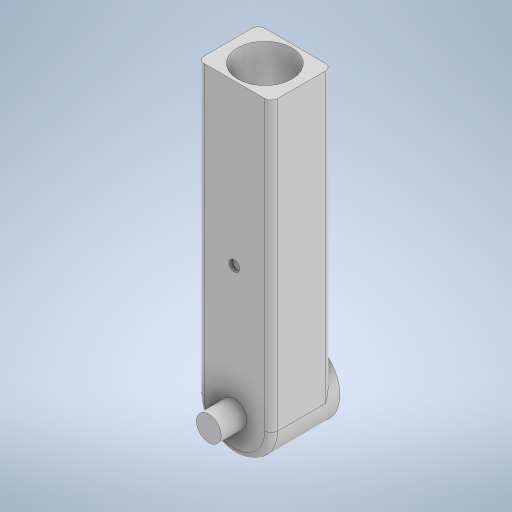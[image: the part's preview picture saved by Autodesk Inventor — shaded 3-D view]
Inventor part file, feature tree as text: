
AUTODESK INVENTOR PART (.ipt)
format: ipt  version: 2023 (Build 270158000, 158)  size: 334,848 bytes
history: native  units: in
note: dims shown in document units (in); Inventor stores cm internally (conversion verified against a paired STEP export)
features: extrude x8, sketch x8, fillet x1
ambient origin geometry x8: Origin, YZ Plane, XZ Plane, XY Plane, X Axis, Y Axis, Z Axis, Center Point
bodies: Solid1 (feature_tree)
feature tree (17):
  extrude  "Extrusion1"  Depth=1.0236in TaperAngle=0.0deg
  extrude  "Extrusion2"  Depth=3.1496in TaperAngle=0.0deg
  extrude  "Extrusion3"  Depth=0.9055in
  extrude  "Extrusion4"  Depth=0.2756in
  extrude  "Extrusion5"  Depth=0.3071in
  extrude  "Extrusion7"  Depth=0.6299in
  extrude  "Extrusion8"  Depth=0.5906in
  fillet  "Fillet2"  Radius=0.1969in
  extrude  "Extrusion9"  Depth=0.0787in
  sketch  "Sketch1"  dims[d0=0.9055in d1=1.0236in d2=0.0in]
  sketch  "Sketch2"  dims[d5=3.5433in d6=0.0in d8=3.1496in d9=0.0in]
  sketch  "Sketch3"  dims[d10=0.3071in d11=0.9055in]
  sketch  "Sketch4"  dims[d12=0.2756in d13=0.0in d15=0.2756in]
  sketch  "Sketch5"  dims[d16=0.0394in d17=0.0in d18=0.3071in]
  sketch  "Sketch7"  dims[d29=0.6693in d31=0.6299in]
  sketch  "Sketch8"  dims[d32=0.5906in d33=0.5906in d34=0.1969in]
  sketch  "Sketch9"  dims[d35=0.1969in d36=0.0787in d37=0.0787in d38=0.0787in d39=0.0787in d40=0.0787in d41=0.0787in d42=0.0787in d43=0.0787in d44=0.315in d45=0.0in d46=0.9055in d47=0.8268in d48=0.0984in d49=0.0in d50=0.0787in d51=0.1299in d52=1.9685in d53=0.0in d54=0.0in]
